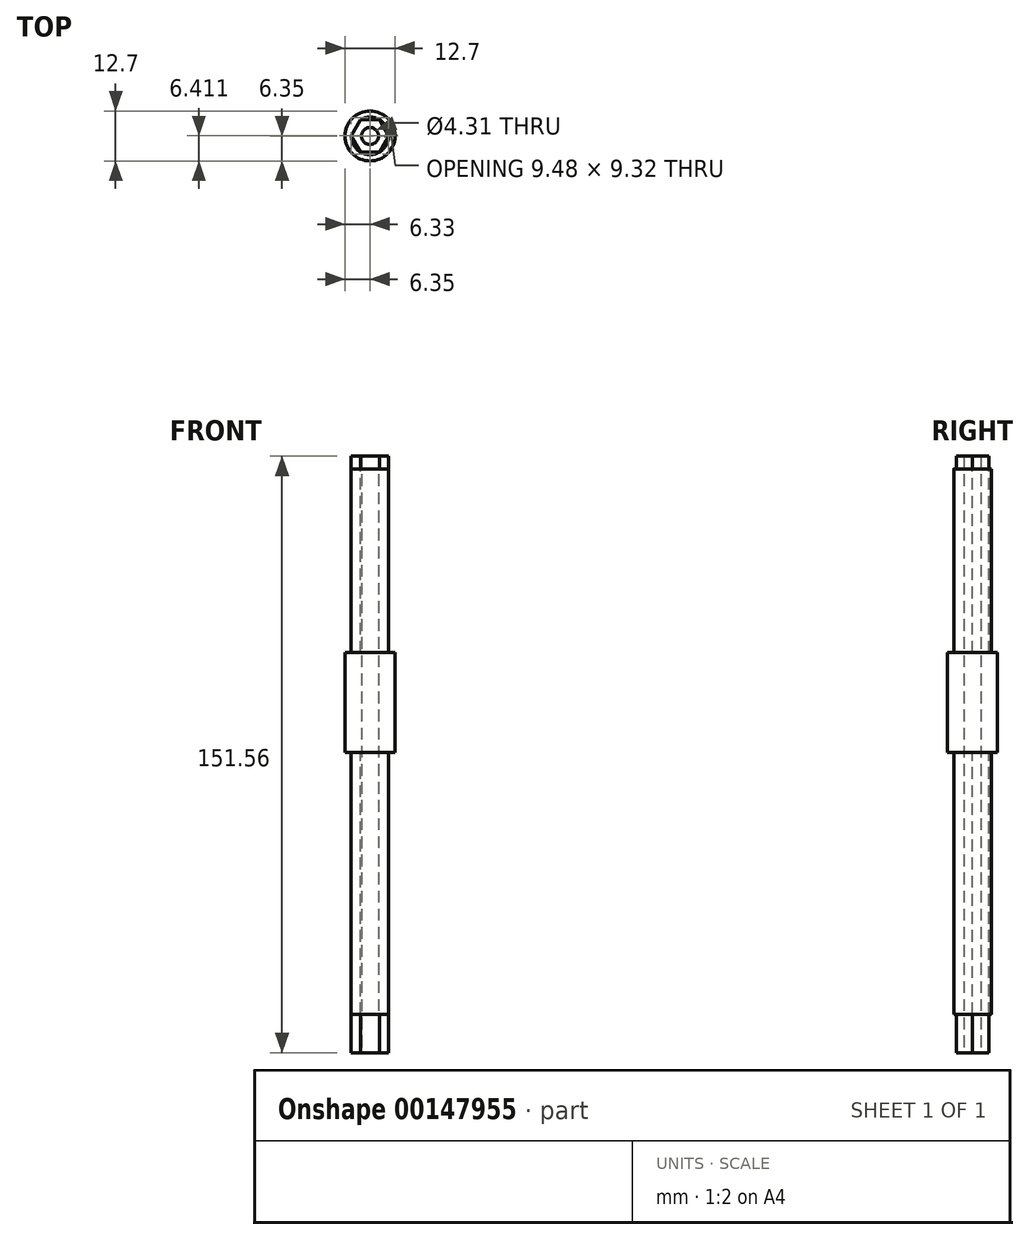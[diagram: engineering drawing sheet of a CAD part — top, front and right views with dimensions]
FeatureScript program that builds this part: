
annotation { "Feature Type Name" : "Feature", "Feature Type Description" : "" }
export const myFeature = defineFeature(function(context is Context, id is Id, definition is map)
    precondition{}
    {
        {
            var Q0;
            Q0=qCreatedBy(makeId("Top.planeOp"),FACE);
            var sketch = newSketch(context, id + "F0", { "sketchPlane" : qUnion([Q0])});
            skCircle(sketch, "E0", {"center": v(0, 0) * mm, "radius": 4.76 * mm});
            skCircle(sketch, "E1", {"center": v(0, 0) * mm, "radius": 2.15 * mm});
            skSolve(sketch);
        }
        {
            var Q0;
            Q0=qSketchRegion(id+"F0",true);
            extrude(context, id + "F1", {"entities" : qUnion([Q0]), "depth" : 138.56 * mm});
        }
        {
            var Q0;
            Q0=makeQuery(id+"F1.opExtrude","CAP_FACE",FACE,{"disambiguationData":[OSD([sQuery(id+"F0.wireOp",EDGE,"E0"),sQuery(id+"F0.wireOp",EDGE,"E1")])],"isStart":true});
            cPlane(context, id + "F2", {"entities" : qUnion([Q0]), "cplaneType" : CPlaneType.OFFSET, "offset" : 9.75 * mm, "width" : 152.4 * mm, "height" : 152.4 * mm});
        }
        {
            var Q0;
            Q0=makeQuery(id+"F1.opExtrude","CAP_FACE",FACE,{"disambiguationData":[OSD([sQuery(id+"F0.wireOp",EDGE,"E0"),sQuery(id+"F0.wireOp",EDGE,"E1")])],"isStart":false});
            var sketch = newSketch(context, id + "F3", { "sketchPlane" : qUnion([Q0])});
            skCircle(sketch, "E2.cCircle", {"center": v(0, 0) * mm, "radius": 4.76 * mm, "construction": true});
            skLineSegment(sketch, "E2.0", {"start": v(2.38, 4.12) * mm, "end": v(4.76, 0) * mm});
            skLineSegment(sketch, "E2.1", {"start": v(4.76, 0) * mm, "end": v(2.38, -4.12) * mm});
            skLineSegment(sketch, "E2.2", {"start": v(2.38, -4.12) * mm, "end": v(-2.38, -4.12) * mm});
            skLineSegment(sketch, "E2.3", {"start": v(-2.38, -4.12) * mm, "end": v(-4.76, 0) * mm});
            skLineSegment(sketch, "E2.4", {"start": v(-4.76, 0) * mm, "end": v(-2.38, 4.12) * mm});
            skLineSegment(sketch, "E2.5", {"start": v(-2.38, 4.12) * mm, "end": v(2.38, 4.12) * mm});
            skCircle(sketch, "E3", {"center": v(0, 0) * mm, "radius": 2.15 * mm});
            skSolve(sketch);
        }
        {
            var Q0;
            Q0=qSketchRegion(id+"F3",true);
            var Q1;
            Q1=qCreatedBy(id+"F2.planeOp",FACE);
            extrude(context, id + "F4", {"entities" : qUnion([Q0]), "operationType" : NewBodyOperationType.ADD, "depth" : 3.25 * mm, "hasSecondDirection" : true, "secondDirectionBound" : SecondDirectionBoundingType.UP_TO_SURFACE, "secondDirectionOppositeDirection" : true, "secondDirectionBoundEntityFace" : qUnion([Q1]), "secondDirectionDepth" : 25.4 * mm});
        }
        {
            var Q0;
            {var subQ0=sQuery(id+"F0.wireOp",EDGE,"E0");var subQ1=makeQuery(id+"F1.opExtrude","CAP_FACE",FACE,{"disambiguationData":[OSD([subQ0,sQuery(id+"F0.wireOp",EDGE,"E1")])],"isStart":false});Q0=makeQuery(id+"F4.boolean.opBoolean","SPLIT",FACE,{"disambiguationData":[TD([makeQuery(id+"F1.opExtrude","SWEPT_FACE",FACE,{"disambiguationData":[OSD([subQ0])]}),subQ1,makeQuery(id+"F4.opExtrude","SWEPT_FACE",FACE,{"disambiguationData":[OSD([sQuery(id+"F3.wireOp",EDGE,"E2.3")])]}),makeQuery(id+"F4.opExtrude","SWEPT_FACE",FACE,{"disambiguationData":[OSD([sQuery(id+"F3.wireOp",EDGE,"E2.4")])]}),makeQuery(id+"F4.opExtrude","SWEPT_FACE",FACE,{"disambiguationData":[OSD([sQuery(id+"F3.wireOp",EDGE,"E2.5")])]})])],"derivedFrom":subQ1});}
            var Q1;
            {var subQ0=sQuery(id+"F0.wireOp",EDGE,"E0");var subQ1=makeQuery(id+"F1.opExtrude","CAP_FACE",FACE,{"disambiguationData":[OSD([subQ0,sQuery(id+"F0.wireOp",EDGE,"E1")])],"isStart":true});Q1=makeQuery(id+"F4.boolean.opBoolean","SPLIT",FACE,{"disambiguationData":[TD([makeQuery(id+"F1.opExtrude","SWEPT_FACE",FACE,{"disambiguationData":[OSD([subQ0])]}),subQ1,makeQuery(id+"F4.opExtrude","SWEPT_FACE",FACE,{"disambiguationData":[OSD([sQuery(id+"F3.wireOp",EDGE,"E2.3")])]}),makeQuery(id+"F4.opExtrude","SWEPT_FACE",FACE,{"disambiguationData":[OSD([sQuery(id+"F3.wireOp",EDGE,"E2.4")])]}),makeQuery(id+"F4.opExtrude","SWEPT_FACE",FACE,{"disambiguationData":[OSD([sQuery(id+"F3.wireOp",EDGE,"E2.5")])]})])],"derivedFrom":subQ1});}
            extrude(context, id + "F5", {"entities" : qUnion([Q0]), "operationType" : NewBodyOperationType.REMOVE, "endBound" : BoundingType.UP_TO_SURFACE, "oppositeDirection" : true, "endBoundEntityFace" : qUnion([Q1]), "depth" : 25.4 * mm});
        }
        {
            var Q0;
            {var subQ0=sQuery(id+"F0.wireOp",EDGE,"E0");var subQ1=makeQuery(id+"F1.opExtrude","CAP_FACE",FACE,{"disambiguationData":[OSD([subQ0,sQuery(id+"F0.wireOp",EDGE,"E1")])],"isStart":false});Q0=makeQuery(id+"F4.boolean.opBoolean","SPLIT",FACE,{"disambiguationData":[TD([makeQuery(id+"F1.opExtrude","SWEPT_FACE",FACE,{"disambiguationData":[OSD([subQ0])]}),subQ1,makeQuery(id+"F4.opExtrude","SWEPT_FACE",FACE,{"disambiguationData":[OSD([sQuery(id+"F3.wireOp",EDGE,"E2.2")])]}),makeQuery(id+"F4.opExtrude","SWEPT_FACE",FACE,{"disambiguationData":[OSD([sQuery(id+"F3.wireOp",EDGE,"E2.3")])]}),makeQuery(id+"F4.opExtrude","SWEPT_FACE",FACE,{"disambiguationData":[OSD([sQuery(id+"F3.wireOp",EDGE,"E2.4")])]})])],"derivedFrom":subQ1});}
            cPlane(context, id + "F6", {"entities" : qUnion([Q0]), "cplaneType" : CPlaneType.OFFSET, "offset" : 46.67 * mm, "oppositeDirection" : true, "width" : 152.4 * mm, "height" : 152.4 * mm});
        }
        {
            var Q0;
            Q0=qCreatedBy(id+"F6.planeOp",FACE);
            var sketch = newSketch(context, id + "F7", { "sketchPlane" : qUnion([Q0])});
            skCircle(sketch, "E4", {"center": v(0, 0) * mm, "radius": 6.35 * mm});
            skCircle(sketch, "E5", {"center": v(0, 0) * mm, "radius": 2.15 * mm});
            skSolve(sketch);
        }
        {
            var Q0;
            Q0=qSketchRegion(id+"F7",true);
            extrude(context, id + "F8", {"entities" : qUnion([Q0]), "operationType" : NewBodyOperationType.ADD, "oppositeDirection" : true, "depth" : 25.4 * mm});
        }
    });
